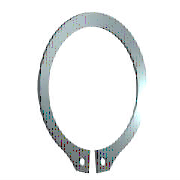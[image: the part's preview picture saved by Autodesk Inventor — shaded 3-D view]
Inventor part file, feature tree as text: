
AUTODESK INVENTOR PART (.ipt)
format: ipt  version: 2015 (Build 190159000, 159)  size: 151,552 bytes
history: native  units: mm (DEFAULTED — no unit token found)
features: sketch x2
ambient origin geometry x8: Origin, YZ Plane, XZ Plane, XY Plane, X Axis, Y Axis, Z Axis, Center Point
bodies: Solid1 (feature_tree)
feature tree (2):
  sketch  "草图2"  dims[d0=0.0mm]
  sketch  "草图3"  dims[d2=1.9mm d4=0.55mm d6=2.2mm d8=1.65mm d10=3.3mm d12=0.44mm d14=0.3mm d15=0.866667mm d16=1.1mm d17=0.0mm d18=1.1mm d20=0.99mm d22=0.99mm d24=1.0mm d26=0.13mm d27=0.0mm d28=18.85mm d32=2.6mm d34=4.0mm d35=1.333333mm d36=2.0mm d37=2.0mm d47=5.133333mm d48=3.6mm d49=0.8mm d51=0.0mm d52=0.0mm d53=0.0mm d54=0.0mm]
